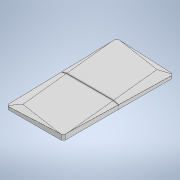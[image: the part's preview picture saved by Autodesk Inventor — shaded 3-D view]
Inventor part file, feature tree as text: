
AUTODESK INVENTOR PART (.ipt)
format: ipt  version: 2020 (Build 240168000, 168)  size: 461,312 bytes
history: native  units: mm
features: sketch x17, extrude x10, plane x6, other x5, pattern_circular x3, fillet x3, move_body x3, sweep x2, chamfer x1, boolean_combine x1, projected_geometry x1
ambient origin geometry x8: Origin, YZ Plane, XZ Plane, XY Plane, X Axis, Y Axis, Z Axis, Center Point
bodies: Solid1 (feature_tree)
feature tree (52):
  other  "Grin.ipt"
  extrude  "Extrusion1"  Depth=85.0mm
  extrude  "Extrusion2"  Depth=5.0mm
  extrude  "Extrusion3"  Depth=4.0mm TaperAngle=0.0deg
  sketch  "Sketch4"  dims[d9=15.0mm d10=10.0mm]
  sketch  "Sketch5"  dims[d13=8.2mm d14=4.0mm]
  sketch  "Sketch6"  dims[d15=10.0mm d16=0.0mm]
  plane  "Work Plane1"
  extrude  "Extrusion4"  Depth=10.0mm
  sketch  "Sketch8"  dims[d18=6.245mm d19=0.0mm d20=20.0mm d21=360.0deg d23=3.0mm d24=2.0mm d25=45.0deg d26=0.1mm]
  plane  "Work Plane2"
  extrude  "Extrusion5"  Depth=4.0mm
  pattern_circular  "Circular Pattern1"  Count=2 Angle=360.0deg
  chamfer  "Chamfer1"  Distance=3.0mm Angle=45.0deg
  fillet  "Fillet1"  Radius=0.1mm
  sketch  "Sketch10"  dims[d29=20.0mm d31=0.75mm d32=20.0mm d34=0.75mm d37=60.0mm d39=360.0deg]
  extrude  "Extrusion9"  Depth=8.828363mm
  move_body  "Move Body4"
  move_body  "Move Body5"
  move_body  "Move Body6"
  boolean_combine  "Combine1"
  fillet  "Fillet3"  Radius=60.0mm
  extrude  "Extrusion10"  Depth=1.0mm TaperAngle=0.0deg
  extrude  "Extrusion6"  Depth=1.0mm TaperAngle=0.0deg
  pattern_circular  "Circular Pattern2"  [2 undecoded]
  extrude  "Extrusion7"  Depth=10.0mm
  plane  "Work Plane4"
  sketch  "Sketch11"  dims[d41=1.5mm d42=1.0mm d43=0.0mm]
  extrude  "Extrusion8"  TaperAngle=0.0deg  [1 undecoded]
  sweep  "Sweep1"
  pattern_circular  "Circular Pattern3"  [2 undecoded]
  fillet  "Fillet2"  [1 undecoded]
  other  "Work Point1"
  other  "Work Point2"
  plane  "Work Plane5"
  sketch  "Sketch14"  dims[d50=4.5mm]
  plane  "Work Plane6"
  sweep  "Sweep2"
  sketch  "Sketch1"  dims[d0=165.0mm d1=85.0mm]
  sketch  "Sketch2"  dims[d2=2.0mm d3=0.0mm d4=5.0mm]
  projected_geometry  "Projected Loop1"
  sketch  "Sketch3"  dims[d5=2.0mm d6=0.0mm d7=4.0mm d8=0.0mm]
  sketch  "Sketch7"  dims[d17=8.2mm]
  sketch  "Sketch9"  dims[d27=29.427878mm d28=8.828363mm]
  plane  "Work Plane3"
  sketch  "Sketch12"  dims[d44=60.0mm d45=360.0deg d47=1.0mm d48=0.0mm]
  sketch  "Sketch13"  dims[d49=90.0deg]
  sketch  "Sketch15"  dims[d51=4.5mm]
  sketch  "Sketch16"  dims[d52=22.75mm d53=4.25mm d54=0.0mm d55=0.0mm]
  other  "Solid1::Grin.ipt_1"
  other  "TaggingFeature2"
  sketch  "Sketch17"  dims[d56=1.5mm d57=0.75mm d58=0.75mm d59=0.0mm d60=0.0mm d61=20.0mm d62=360.0deg d64=0.1mm d65=90.0deg d66=1.0mm d67=1.0mm d68=0.0mm d69=0.0mm d70=1.5mm d71=1.0mm d72=4.5mm d73=1.0mm d74=0.0mm d75=0.0mm d84=25.0mm d85=-15.707963mm d86=10.0mm d87=0.0mm d88=0.0mm d89=0.0mm d90=6.5mm d91=0.0mm d92=17.0mm d93=0.0mm d94=65.0mm d95=0.3mm d96=6.981317mm d97=1.5mm d98=0.5mm d99=0.5mm d100=10.0mm d101=0.0mm]
note: 6 required parameter values undecoded (feature->parameter linkage not recoverable at this tier; creation-order binding heuristic only, values carry confidence <= 0.55)
